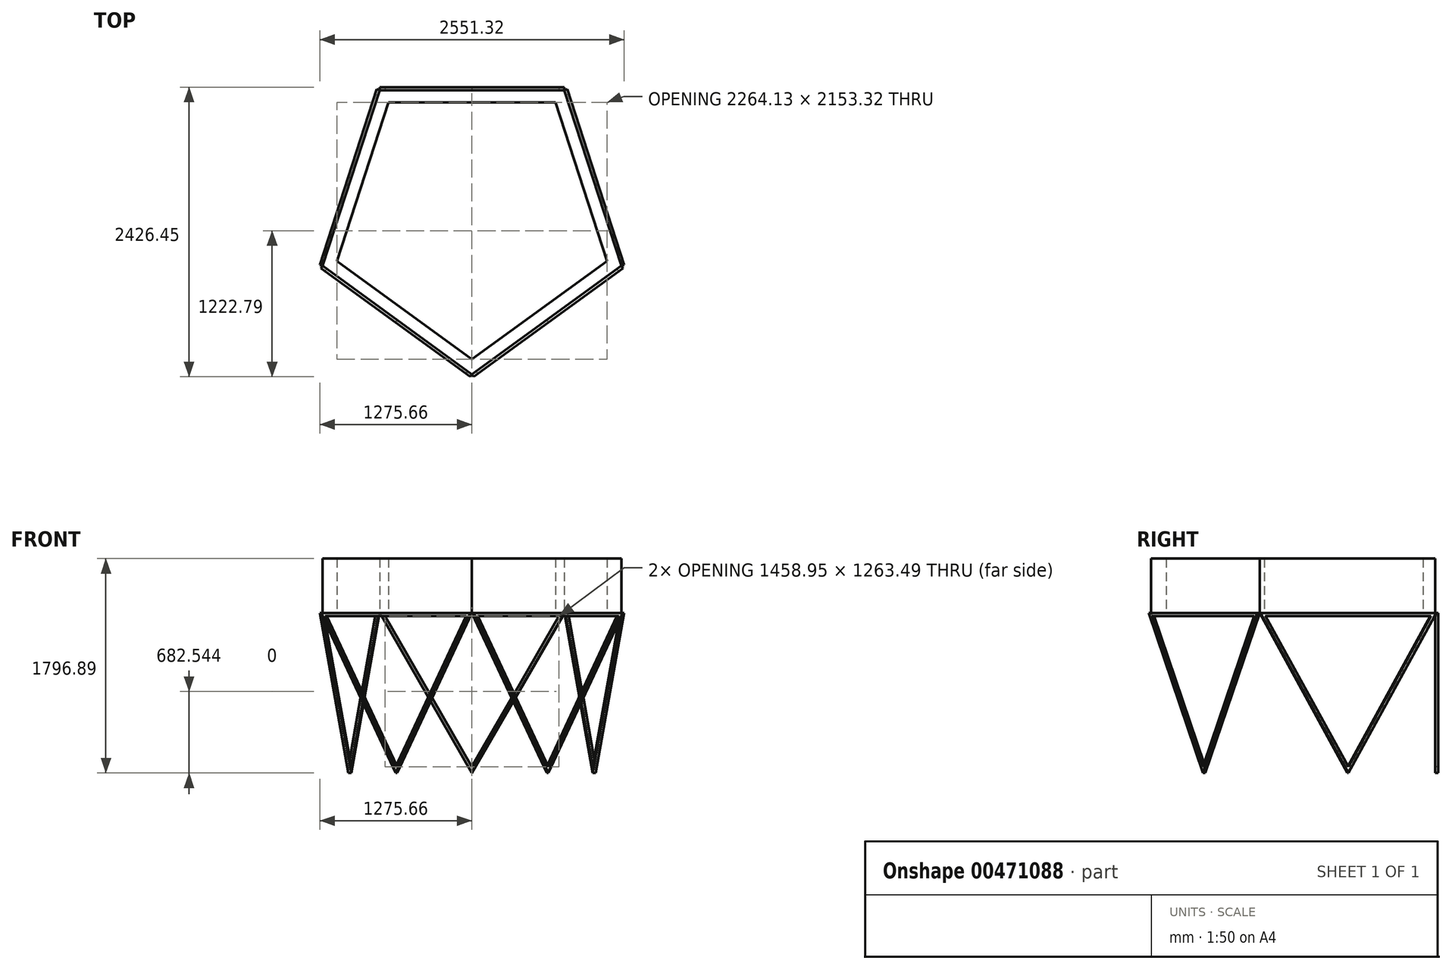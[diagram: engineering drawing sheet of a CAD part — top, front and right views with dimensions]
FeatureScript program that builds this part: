
annotation { "Feature Type Name" : "Feature", "Feature Type Description" : "" }
export const myFeature = defineFeature(function(context is Context, id is Id, definition is map)
    precondition{}
    {
        {
            var Q0;
            Q0=qCreatedBy(makeId("Top.planeOp"),FACE);
            var sketch = newSketch(context, id + "F0", { "sketchPlane" : qUnion([Q0])});
            skCircle(sketch, "E0.cCircle", {"center": v(0, 0) * mm, "radius": 963 * mm, "construction": true});
            skLineSegment(sketch, "E0.0", {"start": v(-699.65, 963) * mm, "end": v(699.65, 963) * mm});
            skLineSegment(sketch, "E0.1", {"start": v(699.65, 963) * mm, "end": v(1132.07, -367.83) * mm});
            skLineSegment(sketch, "E0.2", {"start": v(1132.07, -367.83) * mm, "end": v(0, -1190.32) * mm});
            skLineSegment(sketch, "E0.3", {"start": v(0, -1190.32) * mm, "end": v(-1132.07, -367.83) * mm});
            skLineSegment(sketch, "E0.4", {"start": v(-1132.07, -367.83) * mm, "end": v(-699.65, 963) * mm});
            skPoint(sketch, "E0.0.midPoint", {"position": v(0, 963) * mm});
            skCircle(sketch, "E1.cCircle", {"center": v(0, 0) * mm, "radius": 1064.6 * mm, "construction": true});
            skLineSegment(sketch, "E1.0", {"start": v(-773.47, 1064.6) * mm, "end": v(773.47, 1064.6) * mm});
            skLineSegment(sketch, "E1.1", {"start": v(773.47, 1064.6) * mm, "end": v(1251.5, -406.64) * mm});
            skLineSegment(sketch, "E1.2", {"start": v(1251.5, -406.64) * mm, "end": v(0, -1315.9) * mm});
            skLineSegment(sketch, "E1.3", {"start": v(0, -1315.9) * mm, "end": v(-1251.5, -406.64) * mm});
            skLineSegment(sketch, "E1.4", {"start": v(-1251.5, -406.64) * mm, "end": v(-773.47, 1064.6) * mm});
            skPoint(sketch, "E1.0.midPoint", {"position": v(0, 1064.6) * mm});
            skCircle(sketch, "E2.cCircle", {"center": v(0, 0) * mm, "radius": 366.64 * mm, "construction": true});
            skLineSegment(sketch, "E2.0", {"start": v(-266.38, 366.64) * mm, "end": v(266.38, 366.64) * mm});
            skLineSegment(sketch, "E2.1", {"start": v(266.38, 366.64) * mm, "end": v(431.02, -140.05) * mm});
            skLineSegment(sketch, "E2.2", {"start": v(431.02, -140.05) * mm, "end": v(0, -453.2) * mm});
            skLineSegment(sketch, "E2.3", {"start": v(0, -453.2) * mm, "end": v(-431.02, -140.05) * mm});
            skLineSegment(sketch, "E2.4", {"start": v(-431.02, -140.05) * mm, "end": v(-266.38, 366.64) * mm});
            skPoint(sketch, "E2.0.midPoint", {"position": v(0, 366.64) * mm});
            skSolve(sketch);
        }
        {
            var Q0;
            Q0=makeQuery(id+"F0.imprint","IMPRINT",FACE,{"disambiguationData":[TD([[makeQuery(id+"F0.imprint","IMPRINT",EDGE,{"derivedFrom":sQuery(id+"F0.wireOp",EDGE,"E0.0")}),1.0]])]});
            extrude(context, id + "F1", {"entities" : qUnion([Q0]), "depth" : 457.2 * mm});
        }
        {
            var Q0;
            Q0=makeQuery(id+"F1.opExtrude","SWEPT_FACE",FACE,{"disambiguationData":[OSD([sQuery(id+"F0.wireOp",EDGE,"E1.4")])]});
            var sketch = newSketch(context, id + "F2", { "sketchPlane" : qUnion([Q0])});
            skLineSegment(sketch, "E3", {"start": v(773.47, 0) * mm, "end": v(0, -1339.7) * mm});
            skLineSegment(sketch, "E4", {"start": v(0, -1339.7) * mm, "end": v(-773.47, 0) * mm});
            skLineSegment(sketch, "E5", {"start": v(729.48, -25.4) * mm, "end": v(0, -1288.9) * mm});
            skLineSegment(sketch, "E6", {"start": v(0, -1288.9) * mm, "end": v(-729.48, -25.4) * mm});
            skLineSegment(sketch, "E7", {"start": v(729.48, -25.4) * mm, "end": v(-729.48, -25.4) * mm});
            skSolve(sketch);
        }
        {
            var Q0;
            Q0=makeQuery(id+"F2.imprint","IMPRINT",FACE,{"disambiguationData":[TD([[makeQuery(id+"F2.imprint","IMPRINT",EDGE,{"derivedFrom":sQuery(id+"F2.wireOp",EDGE,"E3")}),-1.0]])]});
            extrude(context, id + "F3", {"entities" : qUnion([Q0]), "depth" : 25.4 * mm});
        }
        {
            var Q0;
            Q0=qCreatedBy(makeId("Right.planeOp"),FACE);
            var sketch = newSketch(context, id + "F4", { "sketchPlane" : qUnion([Q0])});
            skLineSegment(sketch, "E8", {"start": v(0, 0) * mm, "end": v(0, -76.22) * mm});
            skLineSegment(sketch, "E9", {"start": v(0, -76.22) * mm, "end": v(0, -3031.24) * mm, "construction": true});
            skPoint(sketch, "E9.endSnap0", {"position": v(0, -38.11) * mm});
            skSolve(sketch);
        }
        {
            var Q0;
            Q0=makeQuery(id+"F3.opExtrude","SWEPT_BODY",BODY,{"disambiguationData":[OSD([sQuery(id+"F0.wireOp",EDGE,"E1.4"),sQuery(id+"F2.wireOp",EDGE,"E3"),sQuery(id+"F2.wireOp",EDGE,"E4"),sQuery(id+"F2.wireOp",EDGE,"E5"),sQuery(id+"F2.wireOp",EDGE,"E6"),sQuery(id+"F2.wireOp",EDGE,"E7")])]});
            var Q1;
            Q1=sQuery(id+"F4.wireOp",EDGE,"E9");
            circularPattern(context, id + "F5", {"entities" : qUnion([Q0]), "axis" : qUnion([Q1]), "angle" : 360 * degree, "instanceCount" : 5, "equalSpace" : true, "isCentered" : true});
        }
        {
            var Q0;
            Q0=makeQuery(id+"F1.opExtrude","CAP_FACE",FACE,{"disambiguationData":[OSD([sQuery(id+"F0.wireOp",EDGE,"E0.0"),sQuery(id+"F0.wireOp",EDGE,"E0.1"),sQuery(id+"F0.wireOp",EDGE,"E0.2"),sQuery(id+"F0.wireOp",EDGE,"E0.3"),sQuery(id+"F0.wireOp",EDGE,"E0.4"),sQuery(id+"F0.wireOp",EDGE,"E1.0"),sQuery(id+"F0.wireOp",EDGE,"E1.1"),sQuery(id+"F0.wireOp",EDGE,"E1.2"),sQuery(id+"F0.wireOp",EDGE,"E1.3"),sQuery(id+"F0.wireOp",EDGE,"E1.4")])],"isStart":true});
            var sketch = newSketch(context, id + "F6", { "sketchPlane" : qUnion([Q0])});
            skSolve(sketch);
        }
        {
            var Q0;
            Q0=makeQuery(id+"F5.opPattern","COPY",VERTEX,{"derivedFrom":makeQuery(id+"F3.opExtrude","CAP_VERTEX",VERTEX,{"disambiguationData":[OSD([sQuery(id+"F2.wireOp",EDGE,"E3"),sQuery(id+"F2.wireOp",EDGE,"E4")])],"isStart":false}),"instanceName":"-4"});
            var Q1;
            Q1=makeQuery(id+"F5.opPattern","COPY",VERTEX,{"derivedFrom":makeQuery(id+"F3.opExtrude","CAP_VERTEX",VERTEX,{"disambiguationData":[OSD([sQuery(id+"F2.wireOp",EDGE,"E3"),sQuery(id+"F2.wireOp",EDGE,"E4")])],"isStart":false}),"instanceName":"-3"});
            var Q2;
            Q2=makeQuery(id+"F5.opPattern","COPY",VERTEX,{"derivedFrom":makeQuery(id+"F3.opExtrude","CAP_VERTEX",VERTEX,{"disambiguationData":[OSD([sQuery(id+"F2.wireOp",EDGE,"E3"),sQuery(id+"F2.wireOp",EDGE,"E4")])],"isStart":false}),"instanceName":"-2"});
            cPlane(context, id + "F7", {"entities" : qUnion([Q0, Q1, Q2]), "cplaneType" : CPlaneType.THREE_POINT, "offset" : 25.4 * mm, "width" : 152.4 * mm, "height" : 152.4 * mm});
        }
    });
